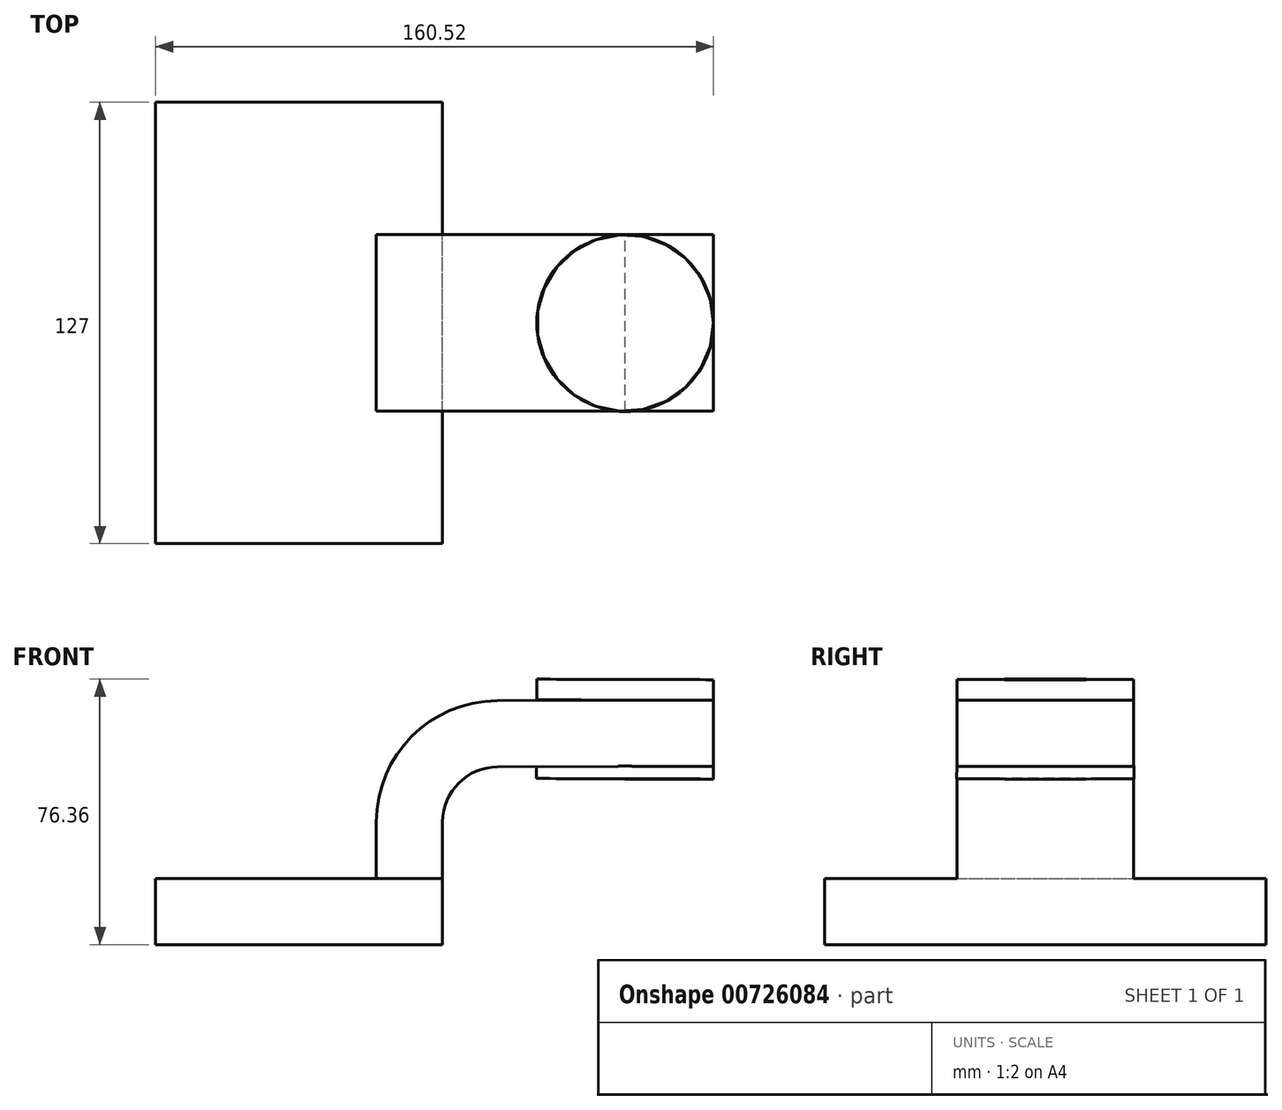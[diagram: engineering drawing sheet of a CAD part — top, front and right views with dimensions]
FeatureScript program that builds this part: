
annotation { "Feature Type Name" : "Feature", "Feature Type Description" : "" }
export const myFeature = defineFeature(function(context is Context, id is Id, definition is map)
    precondition{}
    {
        {
            var Q0;
            Q0=qCreatedBy(makeId("Front.planeOp"),FACE);
            var sketch = newSketch(context, id + "F0", { "sketchPlane" : qUnion([Q0])});
            skLineSegment(sketch, "E0.bottom", {"start": v(41.28, -9.52) * mm, "end": v(-41.28, -9.53) * mm});
            skLineSegment(sketch, "E0.top", {"start": v(41.28, 9.53) * mm, "end": v(-41.28, 9.53) * mm});
            skLineSegment(sketch, "E0.left", {"start": v(41.28, -9.52) * mm, "end": v(41.28, 9.53) * mm});
            skLineSegment(sketch, "E0.right", {"start": v(-41.28, -9.53) * mm, "end": v(-41.28, 9.53) * mm});
            skPoint(sketch, "E0.middle", {"position": v(0, 0) * mm});
            skLineSegment(sketch, "E1", {"start": v(41.28, 9.53) * mm, "end": v(41.28, 25.72) * mm});
            skArc(sketch, "E2", {"start": v(41.27, 25.72) * mm, "mid": v(45.9, 36.92) * mm, "end": v(57.08, 41.6) * mm});
            skLineSegment(sketch, "E3", {"start": v(57.08, 41.6) * mm, "end": v(93.84, 41.76) * mm});
            skLineSegment(sketch, "E4.bottom", {"start": v(119.24, 38.1) * mm, "end": v(68.44, 38.1) * mm});
            skLineSegment(sketch, "E4.top", {"start": v(119.24, 66.68) * mm, "end": v(68.44, 66.68) * mm});
            skLineSegment(sketch, "E4.left", {"start": v(119.24, 38.1) * mm, "end": v(119.24, 66.68) * mm});
            skLineSegment(sketch, "E4.right", {"start": v(68.44, 38.1) * mm, "end": v(68.44, 66.68) * mm});
            skPoint(sketch, "E4.middle", {"position": v(93.84, 52.39) * mm});
            skLineSegment(sketch, "E5.0", {"start": v(57, 60.64) * mm, "end": v(93.76, 60.8) * mm});
            skArc(sketch, "E5.1", {"start": v(22.23, 25.72) * mm, "mid": v(32.4, 50.36) * mm, "end": v(57, 60.64) * mm});
            skLineSegment(sketch, "E5.2", {"start": v(22.22, 9.53) * mm, "end": v(22.22, 25.72) * mm});
            skLineSegment(sketch, "E6", {"start": v(93.84, 66.68) * mm, "end": v(93.76, 38.1) * mm});
            skFitSpline(sketch, "E7", {"points": [v(-41.28, 9.53) * mm, v(-26.77, 33.36) * mm, v(18.7, 62.36) * mm, v(68.44, 66.68) * mm], "startDerivative": vector(39.7, 87.6) * mm, "endDerivative": vector(137.8, -4.54) * mm});
            skLineSegment(sketch, "E8", {"start": v(93.76, 60.8) * mm, "end": v(119.24, 60.73) * mm});
            skLineSegment(sketch, "E9", {"start": v(93.84, 41.76) * mm, "end": v(119.24, 41.76) * mm});
            skLineSegment(sketch, "E10", {"start": v(68.44, 66.68) * mm, "end": v(68.44, 38.1) * mm});
            skLineSegment(sketch, "E11", {"start": v(119.24, 66.68) * mm, "end": v(119.24, 38.1) * mm});
            skLineSegment(sketch, "E12", {"start": v(68.44, 38.1) * mm, "end": v(119.24, 38.1) * mm});
            skLineSegment(sketch, "E13", {"start": v(68.44, 66.68) * mm, "end": v(119.24, 66.68) * mm});
            skSolve(sketch);
        }
        {
            var Q0;
            Q0=makeQuery(id+"F0.imprint","IMPRINT",FACE,{"disambiguationData":[TD([[makeQuery(id+"F0.imprint","IMPRINT",EDGE,{"derivedFrom":sQuery(id+"F0.wireOp",EDGE,"E0.bottom")}),-1.0]])]});
            extrude(context, id + "F1", {"entities" : qUnion([Q0]), "endBound" : BoundingType.SYMMETRIC, "depth" : 127 * mm, "offsetDistance" : 25.4 * mm});
        }
        {
            var Q0;
            {var subQ5=sQuery(id+"F0.wireOp",EDGE,"E1");Q0=makeQuery(id+"F0.imprint","IMPRINT",FACE,{"disambiguationData":[TD([[makeQuery(id+"F0.imprint","IMPRINT",EDGE,{"derivedFrom":subQ5}),1.0]])]});}
            extrude(context, id + "F2", {"entities" : qUnion([Q0]), "operationType" : NewBodyOperationType.ADD, "endBound" : BoundingType.SYMMETRIC, "depth" : 50.8 * mm, "offsetDistance" : 25.4 * mm});
        }
        {
            var Q0;
            {var subQ0=sQuery(id+"F0.wireOp",EDGE,"E5.1");Q0=makeQuery(id+"F0.imprint","IMPRINT",FACE,{"disambiguationData":[TD([[makeQuery(id+"F0.imprint","IMPRINT",EDGE,{"derivedFrom":subQ0}),1.0]])]});}
            extrude(context, id + "F3", {"entities" : qUnion([Q0]), "operationType" : NewBodyOperationType.ADD, "depth" : 15.88 * mm, "offsetDistance" : 25.4 * mm});
        }
        {
            var Q0;
            {var subQ1=sQuery(id+"F0.wireOp",EDGE,"E3");var subQ7=sQuery(id+"F0.wireOp",EDGE,"E4.right");var subQ9=makeQuery(id+"F0.imprint","INTERSECT",VERTEX,{"derivedFrom":[subQ1,subQ7]});Q0=makeQuery(id+"F0.imprint","IMPRINT",FACE,{"disambiguationData":[TD([[makeQuery(id+"F0.imprint","IMPRINT",EDGE,{"disambiguationData":[TD([[subQ9,-1.0]])],"derivedFrom":subQ1}),1.0]])]});}
            var Q1;
            {var subQ7=sQuery(id+"F0.wireOp",EDGE,"E9");Q1=makeQuery(id+"F0.imprint","IMPRINT",FACE,{"disambiguationData":[TD([[makeQuery(id+"F0.imprint","IMPRINT",EDGE,{"derivedFrom":subQ7}),1.0]])]});}
            extrude(context, id + "F4", {"entities" : qUnion([Q0, Q1]), "operationType" : NewBodyOperationType.ADD, "endBound" : BoundingType.SYMMETRIC, "depth" : 50.8 * mm, "offsetDistance" : 25.4 * mm});
        }
        {
            var Q0;
            {var subQ1=sQuery(id+"F0.wireOp",EDGE,"E9");Q0=makeQuery(id+"F0.imprint","IMPRINT",FACE,{"disambiguationData":[TD([[makeQuery(id+"F0.imprint","IMPRINT",EDGE,{"derivedFrom":subQ1}),-1.0]])]});}
            var Q1;
            {var subQ0=sQuery(id+"F0.wireOp",EDGE,"E11");var subQ1=sQuery(id+"F0.wireOp",EDGE,"E8");var subQ2=makeQuery(id+"F0.imprint","INTERSECT",VERTEX,{"derivedFrom":[subQ1,subQ0]});Q1=makeQuery(id+"F0.imprint","IMPRINT",FACE,{"disambiguationData":[TD([[makeQuery(id+"F0.imprint","IMPRINT",EDGE,{"disambiguationData":[TD([[subQ2,1.0]])],"derivedFrom":subQ1}),1.0]])]});}
            var Q2;
            Q2=sQuery(id+"F0.wireOp",EDGE,"E6");
            revolve(context, id + "F5", {"operationType" : NewBodyOperationType.ADD, "surfaceOperationType" : NewSurfaceOperationType.NEW, "entities" : qUnion([Q0, Q1]), "axis" : qUnion([Q2]), "revolveType" : RevolveType.FULL});
        }
    });
